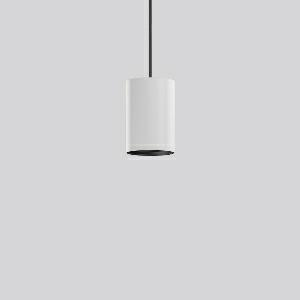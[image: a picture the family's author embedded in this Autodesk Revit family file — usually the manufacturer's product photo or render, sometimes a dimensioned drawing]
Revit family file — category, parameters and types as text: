
# Revit family: deecos_p_maxi_911556_002_76_59e5
name_source: partatom
category: Lighting Fixtures
units: mm (PartAtom-declared; Revit-internal decimal feet)

## family parameters
Cut with Voids When Loaded = No
Host = Face
Light Source = No
Part Type = Normal
Room Calculation Point = No
Round Connector Dimension = Use Diameter
Shared = No

## types (1)
- DEECOS P maxi (1 x LED Modul 920 meat+, 1900 lm, 2000)
    Apparent Load = 33 VA
    Approval mark = CE
    CIE Flux Codes = 96 99 100 100 100
    Color Rendering = 90
    Color Temperature = 2000
    Default Elevation = 1800 mm
    Description = Series: DEECOS P maxi
Cylindrical pendant luminaire. Housing: die-cast aluminium, powder-coated. Canopy made of powder-coated sheet steel with magnetic attachment. Optical assembly with lens made of plastic (polycarbonate) for the best homogeneous light distribution - can be changed without tools. Including special LED for illuminating meat products / Meat plus - intense red. Transparent suspension cable 2 m, can be shortened. High quality converter without flickering and stroboscopic effect. The following accessories can be mounted without use of tools: interchangeable lenses, honeycomb louvre, clear and frosted diffusers, white interchangeable plastic ring. Decorative recessed suspension set available as accessory. 
Colour: traffic white, matt (RAL 9016)
Diameter: 123 mm
Height: 181 mm
Suspension length: 2000 mm
Lamp: LED
Socket: without socket
Colour temperature: meat +
Colour rendering index (CRI): 92
System power: 33 W
Rated luminous flux: 1900 lm
Luminous efficiency: 58 lm/W
Control gear: Converter, dimmable, DALI
Protection class: I
Type of protection: IP 20
    Height = 181 mm
    Lamp = 1 x LED Modul 920 meat+
    Lamp Light Flux = 1900 lm
    Lamp count = 1
    Length = 123 mm
    Lifetime = 50000 h
    Luminous efficacy = 58 lm/W
    Manufacturer = RZB
    ModVariant = No
    Model = 911556.002.76
    Mounting Place = Ceiling
    Mounting Type = Pendant
    Number of Poles = 1
    OnlyDefault = Yes
    Power Factor = 1
    Product Name = DEECOS P maxi
    Product group = Pendant luminaires
    ProductGroupID = 902
    Protection Class = Protection class I
    Protection Degree = IP 20
    RLX_Detail_Level = 1
    RLX_Emergency_Light_Flux = 0 lm
    RLX_Emergency_Type = 0
    RLX_Emergency_Type_DB = No
    RlxData = <blob elided: 35721 chars, md5=3c2c5294>
    Socket = socket
    Standby Power = 0 W
    System Light Flux = 1900 lm
    System Power = 33 W
    Type Comments = Product without accessories
    Type Image = 911480.002.jpg
    URL = http://relux.com
    VarID = ---
    Voltage = 230 V
    Voltage Range = 220-240 V
    Weight = 0.00 kg
    Width = 0 mm  [stored 0 ft]

note: [stored X ft] marks values corroborated as IEEE doubles in the binary element streams (Revit-internal decimal feet)

## geometry (parser evidence)
native form markers: Blend x4, Sweep x10
no freeform markers — native parametric forms only
